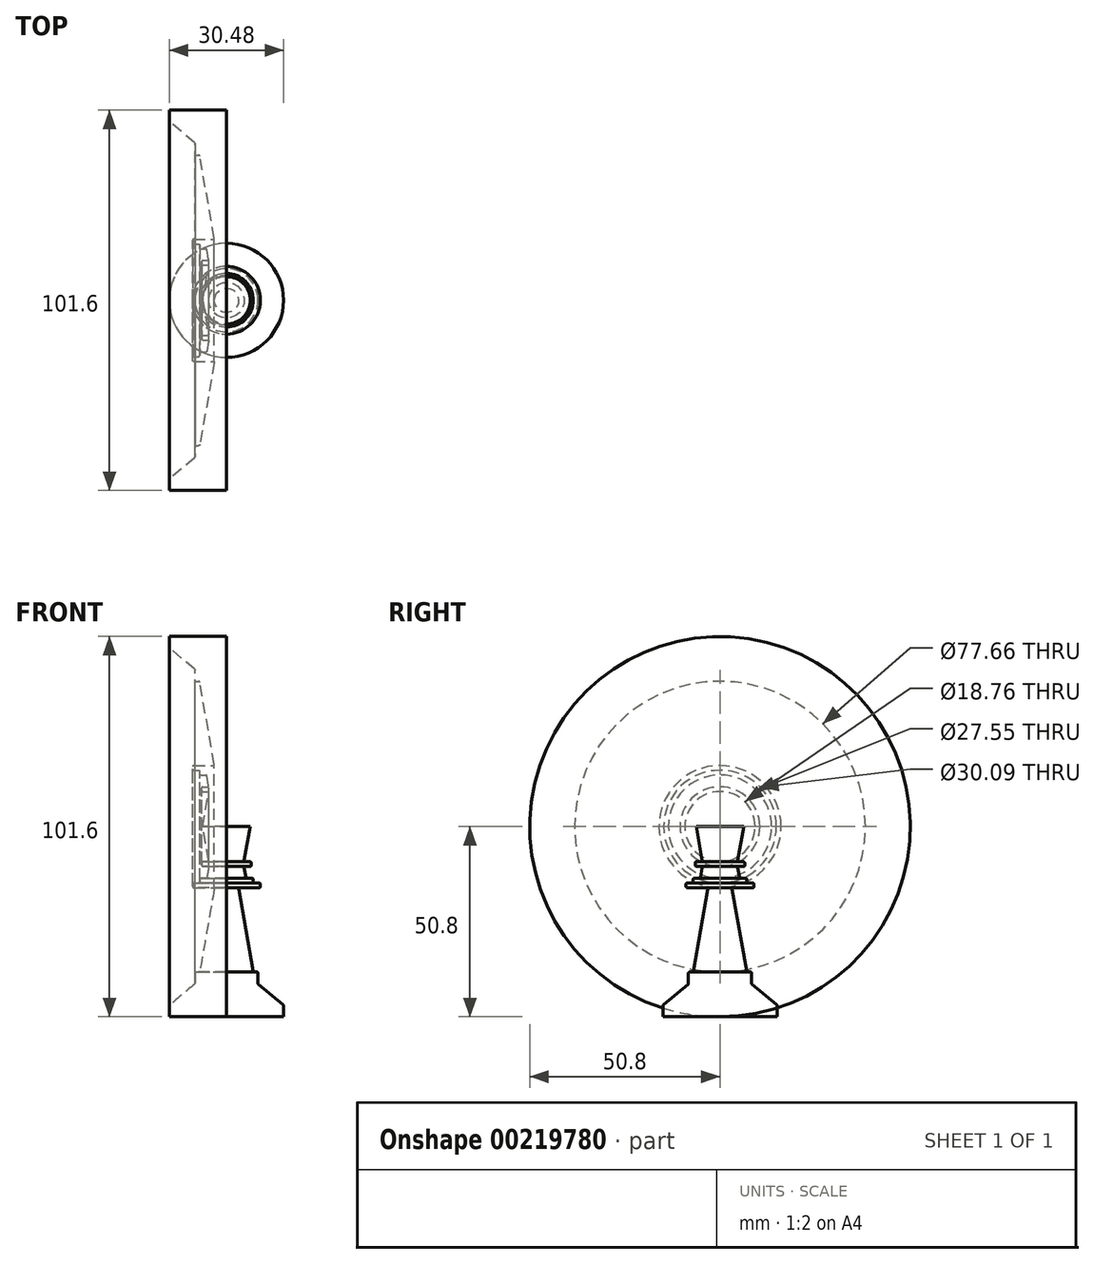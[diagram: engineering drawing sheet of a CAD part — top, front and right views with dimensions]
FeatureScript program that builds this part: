
annotation { "Feature Type Name" : "Feature", "Feature Type Description" : "" }
export const myFeature = defineFeature(function(context is Context, id is Id, definition is map)
    precondition{}
    {
        {
            var Q0;
            Q0=qCreatedBy(makeId("Front.planeOp"),FACE);
            var sketch = newSketch(context, id + "F0", { "sketchPlane" : qUnion([Q0])});
            skLineSegment(sketch, "E0.bottom", {"start": v(0, 0) * mm, "end": v(-15.24, 0) * mm});
            skLineSegment(sketch, "E0.top", {"start": v(0, 50.8) * mm, "end": v(-6.35, 50.8) * mm});
            skLineSegment(sketch, "E0.left", {"start": v(0, 0) * mm, "end": v(0, 50.8) * mm});
            skLineSegment(sketch, "E1", {"start": v(-15.24, 0) * mm, "end": v(-15.24, 2.93) * mm});
            skLineSegment(sketch, "E2", {"start": v(-15.13, 3.18) * mm, "end": v(-8.54, 8.7) * mm});
            skLineSegment(sketch, "E3", {"start": v(-8.43, 8.94) * mm, "end": v(-8.43, 11.65) * mm});
            skLineSegment(sketch, "E4", {"start": v(-8.11, 11.97) * mm, "end": v(-7.43, 11.97) * mm});
            skLineSegment(sketch, "E5", {"start": v(-7.11, 12.23) * mm, "end": v(-3.26, 34.11) * mm});
            skLineSegment(sketch, "E6", {"start": v(-3.57, 34.48) * mm, "end": v(-8.74, 34.48) * mm});
            skLineSegment(sketch, "E7", {"start": v(-9.06, 34.8) * mm, "end": v(-9.06, 35.44) * mm});
            skLineSegment(sketch, "E8", {"start": v(-8.74, 35.75) * mm, "end": v(-7.47, 35.75) * mm});
            skLineSegment(sketch, "E9", {"start": v(-7.15, 36.07) * mm, "end": v(-7.15, 36.7) * mm});
            skLineSegment(sketch, "E10", {"start": v(-6.83, 37.02) * mm, "end": v(-5.51, 37.02) * mm});
            skLineSegment(sketch, "E11", {"start": v(-5.2, 37.29) * mm, "end": v(-4.76, 39.78) * mm});
            skLineSegment(sketch, "E12", {"start": v(-5.07, 40.15) * mm, "end": v(-6.28, 40.15) * mm});
            skLineSegment(sketch, "E13", {"start": v(-6.6, 40.47) * mm, "end": v(-6.6, 41.1) * mm});
            skLineSegment(sketch, "E14", {"start": v(-6.28, 41.42) * mm, "end": v(-5.07, 41.42) * mm});
            skLineSegment(sketch, "E15", {"start": v(-4.76, 41.8) * mm, "end": v(-6.35, 50.8) * mm});
            skPoint(sketch, "E16.visualSharp", {"position": v(-15.24, 3.08) * mm});
            skArc(sketch, "E16.filletArc", {"start": v(-15.13, 3.18) * mm, "mid": v(-15.21, 3.07) * mm, "end": v(-15.24, 2.93) * mm});
            skPoint(sketch, "E17.visualSharp", {"position": v(-8.43, 8.8) * mm});
            skArc(sketch, "E17.filletArc", {"start": v(-8.54, 8.7) * mm, "mid": v(-8.46, 8.8) * mm, "end": v(-8.43, 8.94) * mm});
            skPoint(sketch, "E18.visualSharp", {"position": v(-3.2, 34.48) * mm});
            skArc(sketch, "E18.filletArc", {"start": v(-3.26, 34.11) * mm, "mid": v(-3.33, 34.37) * mm, "end": v(-3.57, 34.48) * mm});
            skPoint(sketch, "E19.visualSharp", {"position": v(-8.43, 11.97) * mm});
            skArc(sketch, "E19.filletArc", {"start": v(-8.11, 11.97) * mm, "mid": v(-8.34, 11.88) * mm, "end": v(-8.43, 11.65) * mm});
            skPoint(sketch, "E20.visualSharp", {"position": v(-7.16, 11.97) * mm});
            skArc(sketch, "E20.filletArc", {"start": v(-7.43, 11.97) * mm, "mid": v(-7.22, 12.04) * mm, "end": v(-7.11, 12.23) * mm});
            skPoint(sketch, "E21.visualSharp", {"position": v(-9.06, 34.48) * mm});
            skArc(sketch, "E21.filletArc", {"start": v(-9.06, 34.8) * mm, "mid": v(-8.96, 34.58) * mm, "end": v(-8.74, 34.48) * mm});
            skPoint(sketch, "E22.visualSharp", {"position": v(-9.06, 35.75) * mm});
            skArc(sketch, "E22.filletArc", {"start": v(-8.74, 35.75) * mm, "mid": v(-8.96, 35.66) * mm, "end": v(-9.06, 35.44) * mm});
            skPoint(sketch, "E23.visualSharp", {"position": v(-7.15, 35.75) * mm});
            skArc(sketch, "E23.filletArc", {"start": v(-7.47, 35.75) * mm, "mid": v(-7.25, 35.85) * mm, "end": v(-7.15, 36.07) * mm});
            skPoint(sketch, "E24.visualSharp", {"position": v(-7.15, 37.02) * mm});
            skArc(sketch, "E24.filletArc", {"start": v(-6.83, 37.02) * mm, "mid": v(-7.06, 36.93) * mm, "end": v(-7.15, 36.7) * mm});
            skPoint(sketch, "E25.visualSharp", {"position": v(-5.25, 37.02) * mm});
            skArc(sketch, "E25.filletArc", {"start": v(-5.51, 37.02) * mm, "mid": v(-5.3, 37.1) * mm, "end": v(-5.2, 37.29) * mm});
            skPoint(sketch, "E26.visualSharp", {"position": v(-4.7, 40.15) * mm});
            skArc(sketch, "E26.filletArc", {"start": v(-4.76, 39.78) * mm, "mid": v(-4.83, 40.04) * mm, "end": v(-5.07, 40.15) * mm});
            skPoint(sketch, "E27.visualSharp", {"position": v(-6.6, 40.15) * mm});
            skArc(sketch, "E27.filletArc", {"start": v(-6.6, 40.47) * mm, "mid": v(-6.5, 40.24) * mm, "end": v(-6.28, 40.15) * mm});
            skPoint(sketch, "E28.visualSharp", {"position": v(-6.6, 41.42) * mm});
            skArc(sketch, "E28.filletArc", {"start": v(-6.28, 41.42) * mm, "mid": v(-6.5, 41.33) * mm, "end": v(-6.6, 41.1) * mm});
            skPoint(sketch, "E29.visualSharp", {"position": v(-4.7, 41.42) * mm});
            skArc(sketch, "E29.filletArc", {"start": v(-5.07, 41.42) * mm, "mid": v(-4.83, 41.53) * mm, "end": v(-4.76, 41.8) * mm});
            skSolve(sketch);
        }
        {
            var Q0;
            Q0=makeQuery(id+"F0.imprint","IMPRINT",FACE,{"disambiguationData":[TD([[makeQuery(id+"F0.imprint","IMPRINT",EDGE,{"derivedFrom":sQuery(id+"F0.wireOp",EDGE,"E0.bottom")}),-1.0]])]});
            var Q1;
            Q1=sQuery(id+"F0.wireOp",EDGE,"E0.top");
            revolve(context, id + "F1", {"entities" : qUnion([Q0]), "axis" : qUnion([Q1]), "revolveType" : RevolveType.FULL});
        }
        {
            var Q0;
            Q0=makeQuery(id+"F0.imprint","IMPRINT",FACE,{"disambiguationData":[TD([[makeQuery(id+"F0.imprint","IMPRINT",EDGE,{"derivedFrom":sQuery(id+"F0.wireOp",EDGE,"E0.bottom")}),-1.0]])]});
            var Q1;
            Q1=sQuery(id+"F0.wireOp",EDGE,"E0.left");
            revolve(context, id + "F2", {"entities" : qUnion([Q0]), "axis" : qUnion([Q1]), "revolveType" : RevolveType.FULL});
        }
    });
